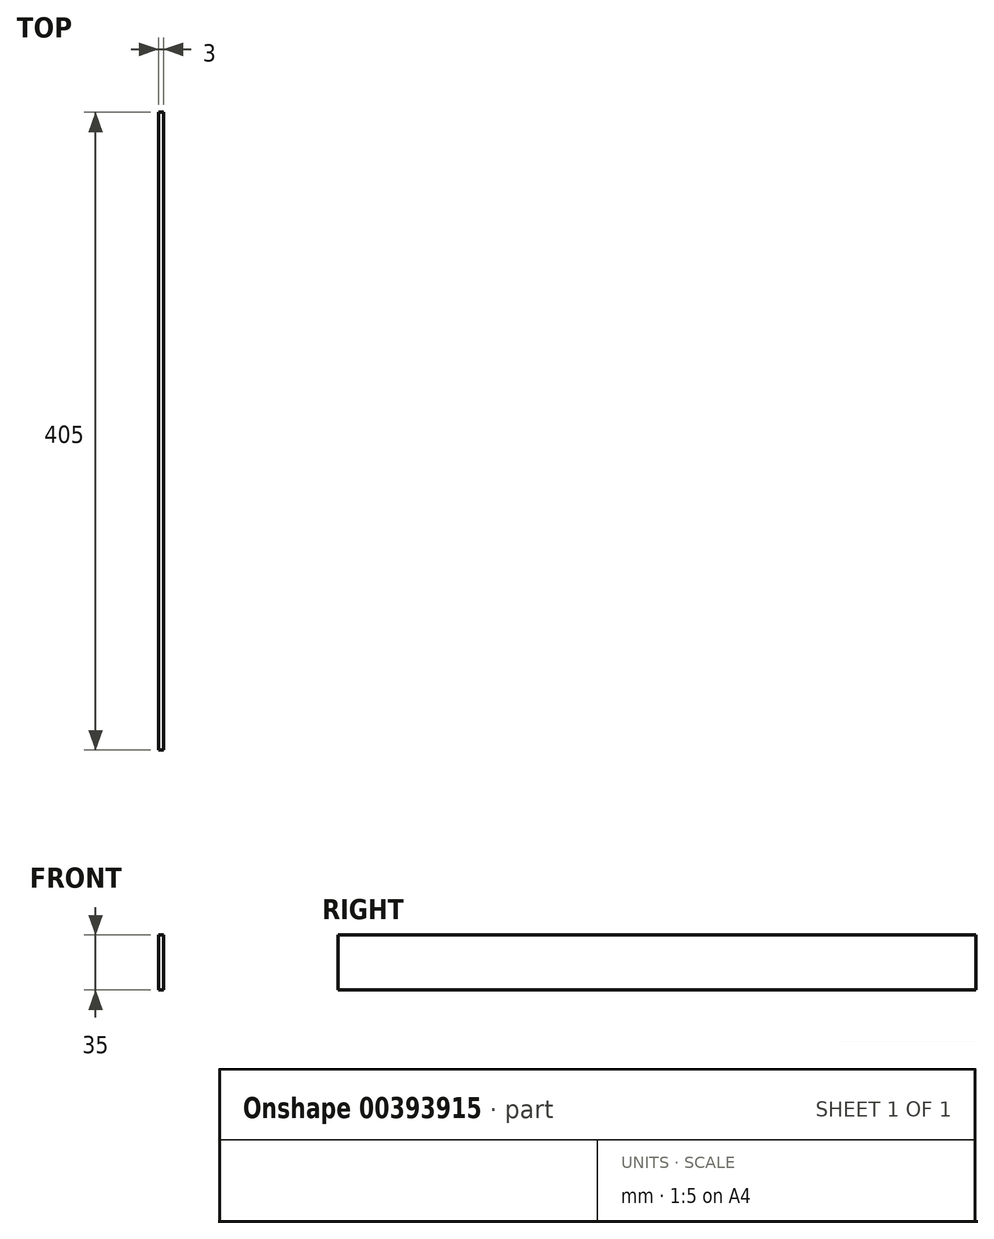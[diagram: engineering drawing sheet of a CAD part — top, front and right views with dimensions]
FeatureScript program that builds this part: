
annotation { "Feature Type Name" : "Feature", "Feature Type Description" : "" }
export const myFeature = defineFeature(function(context is Context, id is Id, definition is map)
    precondition{}
    {
        {
            var Q0;
            Q0=qCreatedBy(makeId("Right.planeOp"),FACE);
            var sketch = newSketch(context, id + "F0", { "sketchPlane" : qUnion([Q0])});
            skLineSegment(sketch, "E0.bottom", {"start": v(202.5, 17.5) * mm, "end": v(-202.5, 17.5) * mm});
            skLineSegment(sketch, "E0.top", {"start": v(202.5, -17.5) * mm, "end": v(-202.5, -17.5) * mm});
            skLineSegment(sketch, "E0.left", {"start": v(202.5, 17.5) * mm, "end": v(202.5, -17.5) * mm});
            skLineSegment(sketch, "E0.right", {"start": v(-202.5, 17.5) * mm, "end": v(-202.5, -17.5) * mm});
            skPoint(sketch, "E0.middle", {"position": v(0, 0) * mm});
            skSolve(sketch);
        }
        {
            var Q0;
            Q0=makeQuery(id+"F0.imprint","IMPRINT",FACE,{"disambiguationData":[TD([[makeQuery(id+"F0.imprint","IMPRINT",EDGE,{"derivedFrom":sQuery(id+"F0.wireOp",EDGE,"E0.bottom")}),1.0]])]});
            extrude(context, id + "F1", {"entities" : qUnion([Q0]), "depth" : 3 * mm});
        }
    });
